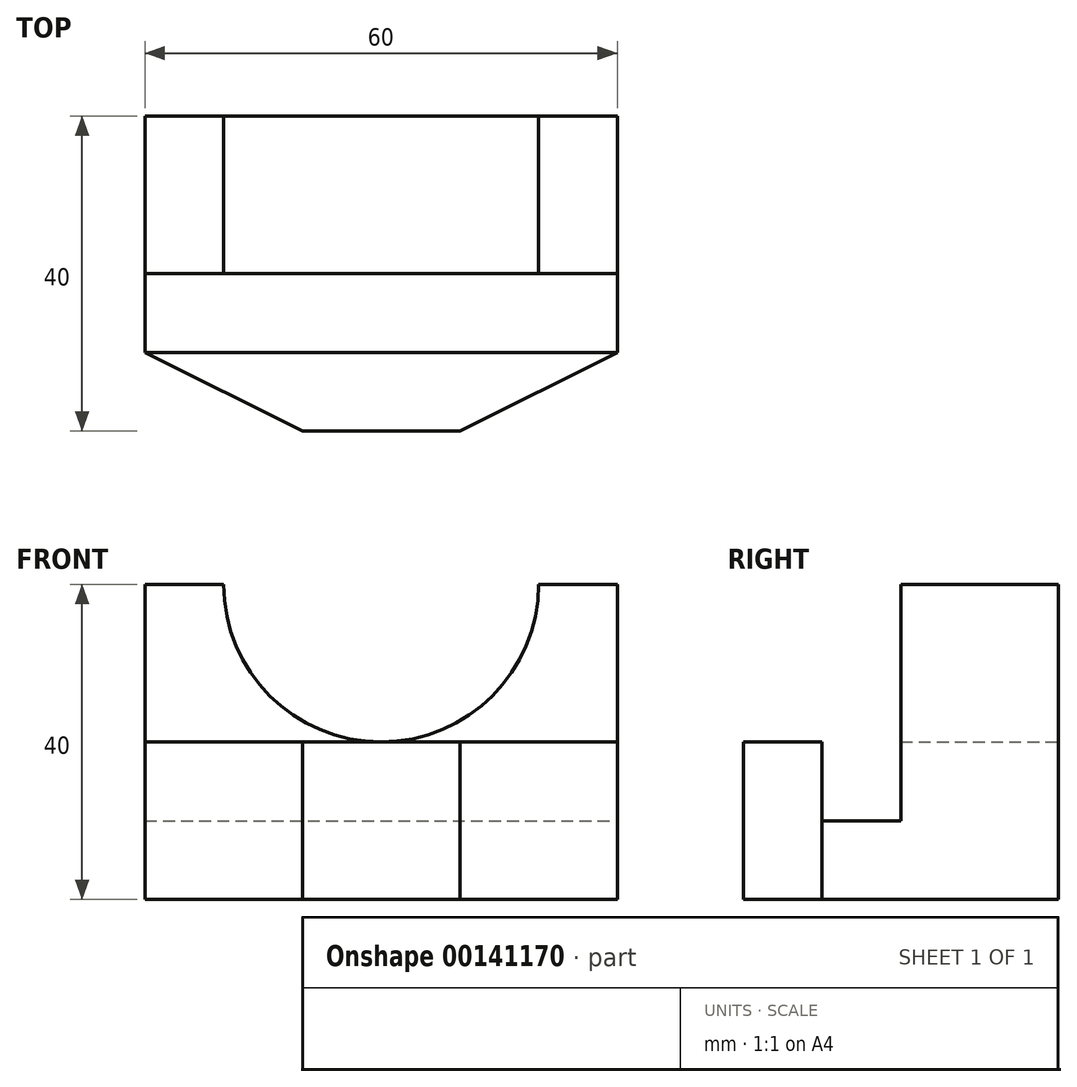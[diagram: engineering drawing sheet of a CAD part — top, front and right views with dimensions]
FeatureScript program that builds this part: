
annotation { "Feature Type Name" : "Feature", "Feature Type Description" : "" }
export const myFeature = defineFeature(function(context is Context, id is Id, definition is map)
    precondition{}
    {
        {
            var Q0;
            Q0=qCreatedBy(makeId("Front.planeOp"),FACE);
            var sketch = newSketch(context, id + "F0", { "sketchPlane" : qUnion([Q0])});
            skLineSegment(sketch, "E0.bottom", {"start": v(-30, -10) * mm, "end": v(30, -10) * mm});
            skLineSegment(sketch, "E0.left", {"start": v(-30, -10) * mm, "end": v(-30, 10) * mm});
            skLineSegment(sketch, "E0.right", {"start": v(30, -10) * mm, "end": v(30, 10) * mm});
            skPoint(sketch, "E0.middle", {"position": v(0, 0) * mm});
            skLineSegment(sketch, "E1", {"start": v(30, 10) * mm, "end": v(30, 30) * mm});
            skLineSegment(sketch, "E2", {"start": v(30, 30) * mm, "end": v(20, 30) * mm});
            skLineSegment(sketch, "E3", {"start": v(-30, 10) * mm, "end": v(-30, 30) * mm});
            skLineSegment(sketch, "E4", {"start": v(-30, 30) * mm, "end": v(-20, 30) * mm});
            skArc(sketch, "E5", {"start": v(-20, 30) * mm, "mid": v(0, 10) * mm, "end": v(20, 30) * mm});
            skSolve(sketch);
        }
        {
            var Q0;
            Q0 = qSketchRegion(id + "F0", true);
            extrude(context, id + "F1", {"entities" : qUnion([Q0]), "depth" : 20 * mm});
        }
        {
            var Q0;
            Q0=makeQuery(id+"F1.opExtrude","CAP_FACE",FACE,{"disambiguationData":[OSD([sQuery(id+"F0.wireOp",EDGE,"E0.bottom"),sQuery(id+"F0.wireOp",EDGE,"E0.left"),sQuery(id+"F0.wireOp",EDGE,"E0.right"),sQuery(id+"F0.wireOp",EDGE,"E1"),sQuery(id+"F0.wireOp",EDGE,"E2"),sQuery(id+"F0.wireOp",EDGE,"E3"),sQuery(id+"F0.wireOp",EDGE,"E4"),sQuery(id+"F0.wireOp",EDGE,"E5")])],"isStart":false});
            var sketch = newSketch(context, id + "F2", { "sketchPlane" : qUnion([Q0])});
            skLineSegment(sketch, "E6.bottom", {"start": v(-30, -10) * mm, "end": v(30, -10) * mm});
            skLineSegment(sketch, "E6.top", {"start": v(-30, 0) * mm, "end": v(30, 0) * mm});
            skLineSegment(sketch, "E6.left", {"start": v(-30, -10) * mm, "end": v(-30, 0) * mm});
            skLineSegment(sketch, "E6.right", {"start": v(30, -10) * mm, "end": v(30, 0) * mm});
            skSolve(sketch);
        }
        {
            var Q0;
            Q0 = qSketchRegion(id + "F2", true);
            extrude(context, id + "F3", {"entities" : qUnion([Q0]), "operationType" : NewBodyOperationType.ADD, "depth" : 10 * mm});
        }
        {
            var Q0;
            Q0=makeQuery(id+"F3.opExtrude","SWEPT_FACE",FACE,{"disambiguationData":[OSD([sQuery(id+"F2.wireOp",EDGE,"E6.top")])]});
            var sketch = newSketch(context, id + "F4", { "sketchPlane" : qUnion([Q0])});
            skLineSegment(sketch, "E7", {"start": v(-30, -30) * mm, "end": v(30, -30) * mm});
            skLineSegment(sketch, "E8", {"start": v(30, -30) * mm, "end": v(10, -40) * mm});
            skLineSegment(sketch, "E9", {"start": v(10, -40) * mm, "end": v(-10, -40) * mm});
            skLineSegment(sketch, "E10", {"start": v(-10, -40) * mm, "end": v(-30, -30) * mm});
            skSolve(sketch);
        }
        {
            var Q0;
            Q0 = qSketchRegion(id + "F4", true);
            extrude(context, id + "F5", {"entities" : qUnion([Q0]), "operationType" : NewBodyOperationType.ADD, "endBound" : BoundingType.SYMMETRIC, "depth" : 20 * mm});
        }
    });
